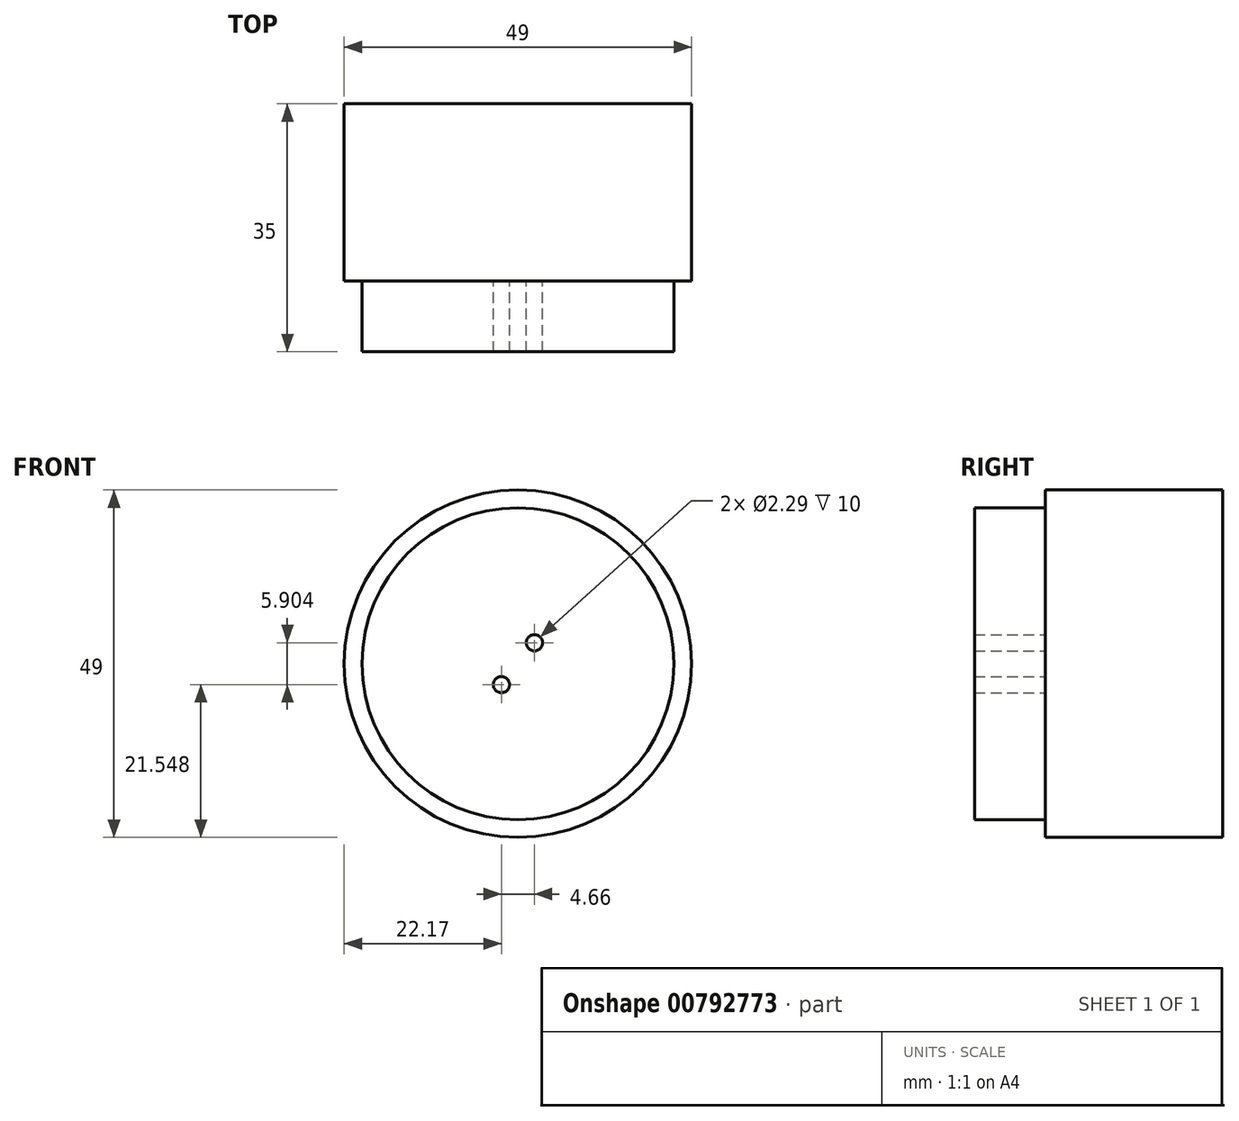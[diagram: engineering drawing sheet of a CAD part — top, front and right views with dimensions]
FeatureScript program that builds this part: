
annotation { "Feature Type Name" : "Feature", "Feature Type Description" : "" }
export const myFeature = defineFeature(function(context is Context, id is Id, definition is map)
    precondition{}
    {
        {
            var Q0;
            Q0=qCreatedBy(makeId("Front.planeOp"),FACE);
            var sketch = newSketch(context, id + "F0", { "sketchPlane" : qUnion([Q0])});
            skCircle(sketch, "E0", {"center": v(0, 0) * mm, "radius": 22 * mm});
            skCircle(sketch, "E1", {"center": v(-2.33, 2.95) * mm, "radius": 1.15 * mm});
            skCircle(sketch, "E2.MirrorC", {"center": v(2.33, 2.95) * mm, "radius": 1.15 * mm});
            skCircle(sketch, "E3.MirrorC", {"center": v(-2.33, -2.95) * mm, "radius": 1.15 * mm});
            skCircle(sketch, "E4.MirrorC", {"center": v(2.33, -2.95) * mm, "radius": 1.15 * mm});
            skCircle(sketch, "E5", {"center": v(0, 0) * mm, "radius": 19.5 * mm});
            skLineSegment(sketch, "E6", {"start": v(2.9, 1.95) * mm, "end": v(19.4, 1.95) * mm});
            skLineSegment(sketch, "E7", {"start": v(2.33, 4.1) * mm, "end": v(2.33, 19.36) * mm});
            skLineSegment(sketch, "E8.MirrorCS", {"start": v(2.9, -1.95) * mm, "end": v(19.4, -1.95) * mm});
            skLineSegment(sketch, "E9.MirrorCS", {"start": v(2.33, -4.1) * mm, "end": v(2.33, -19.36) * mm});
            skLineSegment(sketch, "E10.MirrorCS", {"start": v(-2.33, 4.1) * mm, "end": v(-2.33, 19.36) * mm});
            skLineSegment(sketch, "E11.MirrorCS", {"start": v(-2.9, 1.95) * mm, "end": v(-19.4, 1.95) * mm});
            skLineSegment(sketch, "E12.MirrorCS", {"start": v(-2.9, -1.95) * mm, "end": v(-19.4, -1.95) * mm});
            skLineSegment(sketch, "E13.MirrorCS", {"start": v(-2.33, -4.1) * mm, "end": v(-2.33, -19.36) * mm});
            skSolve(sketch);
        }
        {
            var Q0;
            Q0=qCreatedBy(makeId("Front.planeOp"),FACE);
            var Q1;
            Q1 = qBodyType(qCreatedBy(id + "FuwyYvlLsSzMg0o_1" ,EDGE), BodyType.WIRE);
            cPlane(context, id + "F1", {"entities" : qUnion([Q0, Q1]), "cplaneType" : CPlaneType.OFFSET, "offset" : 15 * mm, "width" : 150 * mm, "height" : 150 * mm});
        }
        {
            var Q0;
            Q0=makeQuery(id+"F0.imprint","IMPRINT",FACE,{"disambiguationData":[TD([[makeQuery(id+"F0.imprint","IMPRINT",EDGE,{"derivedFrom":sQuery(id+"F0.wireOp",EDGE,"E0")}),1.0]])]});
            extrude(context, id + "F2", {"entities" : qUnion([Q0]), "depth" : 25 * mm, "offsetDistance" : 25 * mm});
        }
        {
            var Q0;
            {var subQ0=sQuery(id+"F0.wireOp",EDGE,"E10.MirrorCS");Q0=makeQuery(id+"F0.imprint","IMPRINT",FACE,{"disambiguationData":[TD([[makeQuery(id+"F0.imprint","IMPRINT",EDGE,{"derivedFrom":subQ0}),1.0]])]});}
            var Q1;
            {var subQ0=sQuery(id+"F0.wireOp",EDGE,"E6");Q1=makeQuery(id+"F0.imprint","IMPRINT",FACE,{"disambiguationData":[TD([[makeQuery(id+"F0.imprint","IMPRINT",EDGE,{"derivedFrom":subQ0}),1.0]])]});}
            var Q2;
            {var subQ1=sQuery(id+"F0.wireOp",EDGE,"E6");Q2=makeQuery(id+"F0.imprint","IMPRINT",FACE,{"disambiguationData":[TD([[makeQuery(id+"F0.imprint","IMPRINT",EDGE,{"derivedFrom":subQ1}),-1.0]])]});}
            var Q3;
            {var subQ0=sQuery(id+"F0.wireOp",EDGE,"E12.MirrorCS");Q3=makeQuery(id+"F0.imprint","IMPRINT",FACE,{"disambiguationData":[TD([[makeQuery(id+"F0.imprint","IMPRINT",EDGE,{"derivedFrom":subQ0}),1.0]])]});}
            var Q4;
            {var subQ0=sQuery(id+"F0.wireOp",EDGE,"E8.MirrorCS");Q4=makeQuery(id+"F0.imprint","IMPRINT",FACE,{"disambiguationData":[TD([[makeQuery(id+"F0.imprint","IMPRINT",EDGE,{"derivedFrom":subQ0}),-1.0]])]});}
            var Q5;
            {var subQ0=sQuery(id+"F0.wireOp",EDGE,"E4.MirrorC");var subQ1=makeQuery(id+"F0.imprint","INTERSECT",VERTEX,{"derivedFrom":[subQ0,sQuery(id+"F0.wireOp",EDGE,"E8.MirrorCS")]});Q5=makeQuery(id+"F0.imprint","IMPRINT",FACE,{"disambiguationData":[TD([[makeQuery(id+"F0.imprint","IMPRINT",EDGE,{"disambiguationData":[TD([[subQ1,1.0]])],"derivedFrom":subQ0}),1.0]])]});}
            var Q6;
            {var subQ0=sQuery(id+"F0.wireOp",EDGE,"E2.MirrorC");var subQ1=makeQuery(id+"F0.imprint","INTERSECT",VERTEX,{"derivedFrom":[subQ0,sQuery(id+"F0.wireOp",EDGE,"E6")]});Q6=makeQuery(id+"F0.imprint","IMPRINT",FACE,{"disambiguationData":[TD([[makeQuery(id+"F0.imprint","IMPRINT",EDGE,{"disambiguationData":[TD([[subQ1,1.0]])],"derivedFrom":subQ0}),-1.0]])]});}
            var Q7;
            {var subQ0=sQuery(id+"F0.wireOp",EDGE,"E1");var subQ1=makeQuery(id+"F0.imprint","INTERSECT",VERTEX,{"derivedFrom":[subQ0,sQuery(id+"F0.wireOp",EDGE,"E10.MirrorCS")]});Q7=makeQuery(id+"F0.imprint","IMPRINT",FACE,{"disambiguationData":[TD([[makeQuery(id+"F0.imprint","IMPRINT",EDGE,{"disambiguationData":[TD([[subQ1,-1.0]])],"derivedFrom":subQ0}),1.0]])]});}
            var Q8;
            {var subQ0=sQuery(id+"F0.wireOp",EDGE,"E3.MirrorC");var subQ1=makeQuery(id+"F0.imprint","INTERSECT",VERTEX,{"derivedFrom":[subQ0,sQuery(id+"F0.wireOp",EDGE,"E12.MirrorCS")]});Q8=makeQuery(id+"F0.imprint","IMPRINT",FACE,{"disambiguationData":[TD([[makeQuery(id+"F0.imprint","IMPRINT",EDGE,{"disambiguationData":[TD([[subQ1,1.0]])],"derivedFrom":subQ0}),-1.0]])]});}
            extrude(context, id + "F3", {"entities" : qUnion([Q0, Q1, Q2, Q3, Q4, Q5, Q6, Q7, Q8]), "operationType" : NewBodyOperationType.ADD, "depth" : 25 * mm, "offsetDistance" : 25 * mm});
        }
        {
            var Q0;
            Q0=qCreatedBy(id+"F1.planeOp",FACE);
            var sketch = newSketch(context, id + "F4", { "sketchPlane" : qUnion([Q0])});
            skCircle(sketch, "E14", {"center": v(0, 0) * mm, "radius": 24.5 * mm});
            skSolve(sketch);
        }
        {
            var Q0;
            Q0 = qSketchRegion(id + "F4", true);
            extrude(context, id + "F5", {"entities" : qUnion([Q0]), "operationType" : NewBodyOperationType.ADD, "oppositeDirection" : true, "depth" : 25 * mm, "offsetDistance" : 25 * mm});
        }
    });
